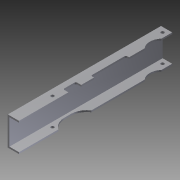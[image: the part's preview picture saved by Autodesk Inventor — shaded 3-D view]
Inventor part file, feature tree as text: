
AUTODESK INVENTOR PART (.ipt)
format: ipt  version: 2012 (Build 160160000, 160)  size: 142,848 bytes
history: native  units: in
note: dims shown in document units (in); Inventor stores cm internally (conversion verified against a paired STEP export)
features: extrude x3, sketch x3, fillet x1
ambient origin geometry x8: Origin, YZ Plane, XZ Plane, XY Plane, X Axis, Y Axis, Z Axis, Center Point
bodies: Solid1 (feature_tree)
feature tree (7):
  extrude  "Extrusion1"  Depth=0.125in
  extrude  "Extrusion2"  Depth=2.25in
  extrude  "Extrusion3"  Depth=12.0in TaperAngle=0.0deg
  fillet  "Fillet1"  Radius=0.125in
  sketch  "Sketch1"  dims[d0=0.125in d1=0.125in]
  sketch  "Sketch2"  dims[d2=0.125in d3=2.25in]
  sketch  "Sketch3"  dims[d4=0.875in d5=12.0in d6=0.0in d9=0.125in d10=0.0in d11=3.375in d12=2.75in d13=0.25in d14=7.125in d15=1.0in d16=0.45in d17=1.25in d18=0.5in d19=7.375in d20=0.3125in d21=0.125in d22=0.0in d23=0.125in d24=1.0in d25=1.625in d26=1.5in d27=0.5in d28=0.375in d29=0.25in d30=9.0in]
